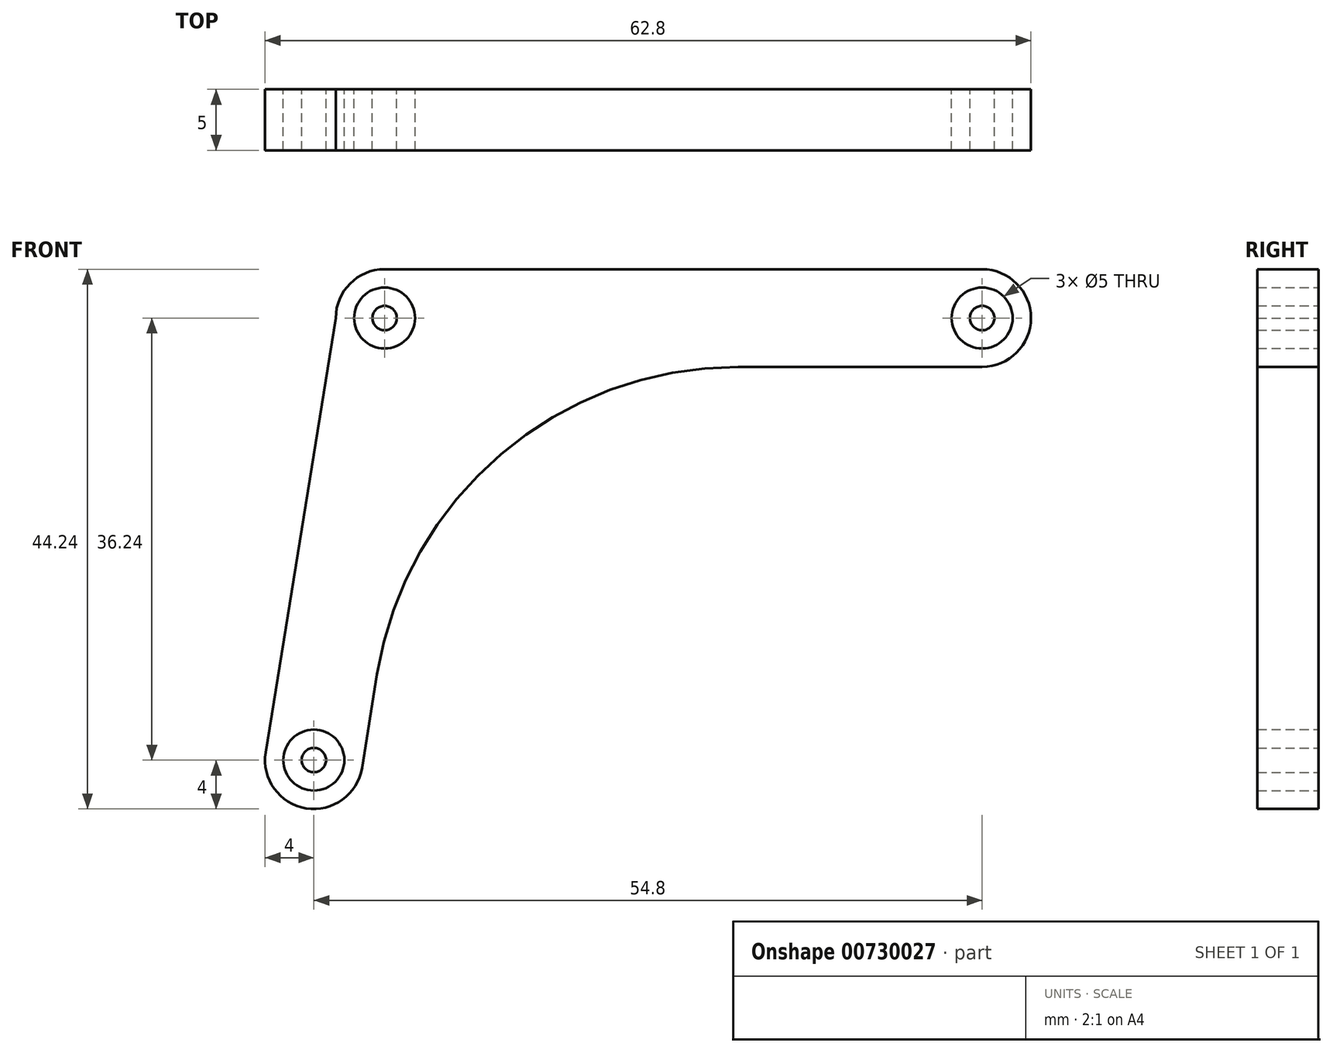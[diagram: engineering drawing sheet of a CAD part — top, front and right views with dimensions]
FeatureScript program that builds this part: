
annotation { "Feature Type Name" : "Feature", "Feature Type Description" : "" }
export const myFeature = defineFeature(function(context is Context, id is Id, definition is map)
    precondition{}
    {
        {
            var Q0;
            Q0=qCreatedBy(makeId("Front.planeOp"),FACE);
            var sketch = newSketch(context, id + "F0", { "sketchPlane" : qUnion([Q0])});
            skCircle(sketch, "E0", {"center": v(0, 0) * mm, "radius": 2.5 * mm});
            skArc(sketch, "E1", {"start": v(0, 4) * mm, "mid": v(-2.83, 2.83) * mm, "end": v(-4, 0) * mm});
            skArc(sketch, "E2", {"start": v(-9.75, -35.6) * mm, "mid": v(-6.44, -40.19) * mm, "end": v(-1.85, -36.88) * mm});
            skLineSegment(sketch, "E3", {"start": v(-4, 0) * mm, "end": v(-9.75, -35.6) * mm});
            skArc(sketch, "E4", {"start": v(49, -4) * mm, "mid": v(53, 0) * mm, "end": v(49, 4) * mm});
            skLineSegment(sketch, "E5", {"start": v(0, 4) * mm, "end": v(49, 4) * mm});
            skLineSegment(sketch, "E6.0", {"start": v(3.9, -1.28) * mm, "end": v(-1.85, -36.88) * mm, "construction": true});
            skLineSegment(sketch, "E7.0", {"start": v(0, -4) * mm, "end": v(49, -4) * mm, "construction": true});
            skLineSegment(sketch, "E8", {"start": v(49, -4) * mm, "end": v(29, -4) * mm});
            skLineSegment(sketch, "E9", {"start": v(-1.85, -36.88) * mm, "end": v(-0.61, -29.22) * mm});
            skArc(sketch, "E10", {"start": v(29, -4) * mm, "mid": v(9.55, -11.16) * mm, "end": v(-0.61, -29.22) * mm});
            skCircle(sketch, "E11", {"center": v(0, 0) * mm, "radius": 1 * mm});
            skCircle(sketch, "E12", {"center": v(-5.8, -36.24) * mm, "radius": 2.5 * mm});
            skCircle(sketch, "E13", {"center": v(-5.8, -36.24) * mm, "radius": 1 * mm});
            skCircle(sketch, "E14", {"center": v(49, 0) * mm, "radius": 2.5 * mm});
            skCircle(sketch, "E15", {"center": v(49, 0) * mm, "radius": 1 * mm});
            skSolve(sketch);
        }
        {
            var Q0;
            Q0 = qSketchRegion(id + "F0", true);
            var Q1;
            Q1=makeQuery(id+"F0.imprint","IMPRINT",FACE,{"disambiguationData":[TD([[makeQuery(id+"F0.imprint","IMPRINT",EDGE,{"derivedFrom":sQuery(id+"F0.wireOp",EDGE,"E11")}),1.0]])]});
            var Q2;
            Q2=makeQuery(id+"F0.imprint","IMPRINT",FACE,{"disambiguationData":[TD([[makeQuery(id+"F0.imprint","IMPRINT",EDGE,{"derivedFrom":sQuery(id+"F0.wireOp",EDGE,"E13")}),1.0]])]});
            var Q3;
            Q3=makeQuery(id+"F0.imprint","IMPRINT",FACE,{"disambiguationData":[TD([[makeQuery(id+"F0.imprint","IMPRINT",EDGE,{"derivedFrom":sQuery(id+"F0.wireOp",EDGE,"E15")}),1.0]])]});
            extrude(context, id + "F1", {"entities" : qUnion([Q0, Q1, Q2, Q3]), "depth" : 5 * mm, "offsetDistance" : 25 * mm});
        }
    });
